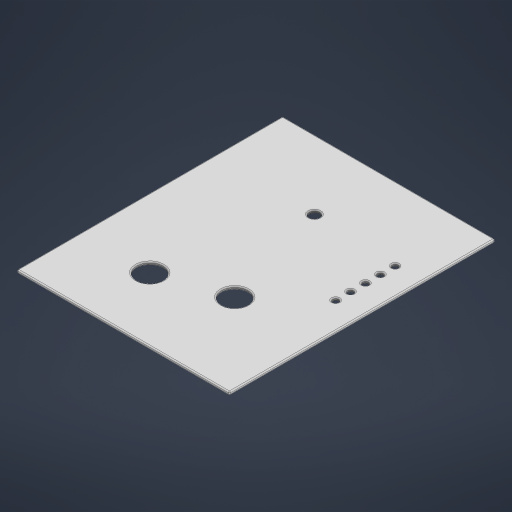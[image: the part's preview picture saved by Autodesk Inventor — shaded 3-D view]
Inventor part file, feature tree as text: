
AUTODESK INVENTOR PART (.ipt)
format: ipt  version: 2023 (Build 270158000, 158)  size: 265,216 bytes
history: native  units: mm
features: extrude x1, fillet x1, other x1
ambient origin geometry x8: Origin, YZ Plane, XZ Plane, XY Plane, X Axis, Y Axis, Z Axis, Center Point
bodies: Solid1 (feature_tree)
feature tree (3):
  extrude  "nor"  Depth=200.0mm
  fillet  "Fillet1"  Radius=250.0mm
  other  "page_lines"
